# Revit family: Legrand Cabinet XL³ 400 Metal
name_source: partatom
category: Equipement électrique
units: mm (PartAtom-declared; Revit-internal decimal feet)

## family parameters
Basée sur le plan de construction = Non
Configuration du panneau = Deux colonnes, circuits au sein
Cote de connecteur circulaire = Utiliser le diamètre
Couper avec des vides une fois chargée = Non
Numéro OmniClass = 23.80.30.11.17
Partagée = Non
Point de calcul de pièce = Non
Titre OmniClass = Distribution Boards and Control Panels
Toujours verticalement = Oui
Type d'élément = Tableau de raccordement

## types (8) — shared parameters
Fabricant = Legrand
Finish = Epoxipolyester paint deposited by electrostatic powder
General Conditions of Use = https://export.legrand.com
ICW (until) (kA) = 25
IK with door = 08
IK without door = 07
IN max (A) = 400
IP with door = 40
IP without door = 30
IPK (kA) = 52.5
Material = Steel
Material corner = Plastic
Modèle = XL³ 400 Metal
RAL = 7035
URL = https://www.legrand.fr
depth (mm) = 200 mm  [stored 0.656168 ft]
depth installation zone = 750 mm  [stored 2.46063 ft]
width (mm) = 575 mm  [stored 1.88648 ft]
width installation zone = 1245 mm
zero-valued in all types: Elévation par défaut

## per-type parameters (varying)
| type | handle Board | handle Cabinet | height | height installation zone | height total (mm) | level Cabinet | level installation zone | plinth |
| 020103-020273 | Non | Oui | 600 mm | 600 mm | 600 mm | 0 mm  [stored 0 ft] | 5 mm  [stored 0.0164042 ft] | Non |
| 020118-020278 | Oui | Non | 1500 mm  [stored 4.92126 ft] | 1600 mm  [stored 5.24934 ft] | 1600 mm  [stored 5.24934 ft] | 100 mm  [stored 0.328084 ft] | 0 mm  [stored 0 ft] | Oui |
| 020104-020274 | Non | Oui | 750 mm  [stored 2.46063 ft] | 750 mm  [stored 2.46063 ft] | 750 mm  [stored 2.46063 ft] | 0 mm  [stored 0 ft] | 5 mm  [stored 0.0164042 ft] | Non |
| 020105-020275 | Non | Oui | 900 mm  [stored 2.95276 ft] | 900 mm  [stored 2.95276 ft] | 900 mm  [stored 2.95276 ft] | 0 mm  [stored 0 ft] | 5 mm  [stored 0.0164042 ft] | Non |
| 020106-020276 | Non | Oui | 1050 mm | 1050 mm | 1050 mm | 0 mm  [stored 0 ft] | 5 mm  [stored 0.0164042 ft] | Non |
| 020107-020277 | Non | Oui | 1200 mm | 1200 mm | 1200 mm | 0 mm  [stored 0 ft] | 5 mm  [stored 0.0164042 ft] | Non |
| 020108-020278 | Non | Oui | 1500 mm  [stored 4.92126 ft] | 1500 mm  [stored 4.92126 ft] | 1500 mm  [stored 4.92126 ft] | 0 mm  [stored 0 ft] | 5 mm  [stored 0.0164042 ft] | Non |
| 020119-020279 | Oui | Non | 1800 mm  [stored 5.90551 ft] | 1900 mm  [stored 6.2336 ft] | 1900 mm  [stored 6.2336 ft] | 100 mm  [stored 0.328084 ft] | 0 mm  [stored 0 ft] | Oui |

note: [stored X ft] marks values corroborated as IEEE doubles in the binary element streams (Revit-internal decimal feet)
